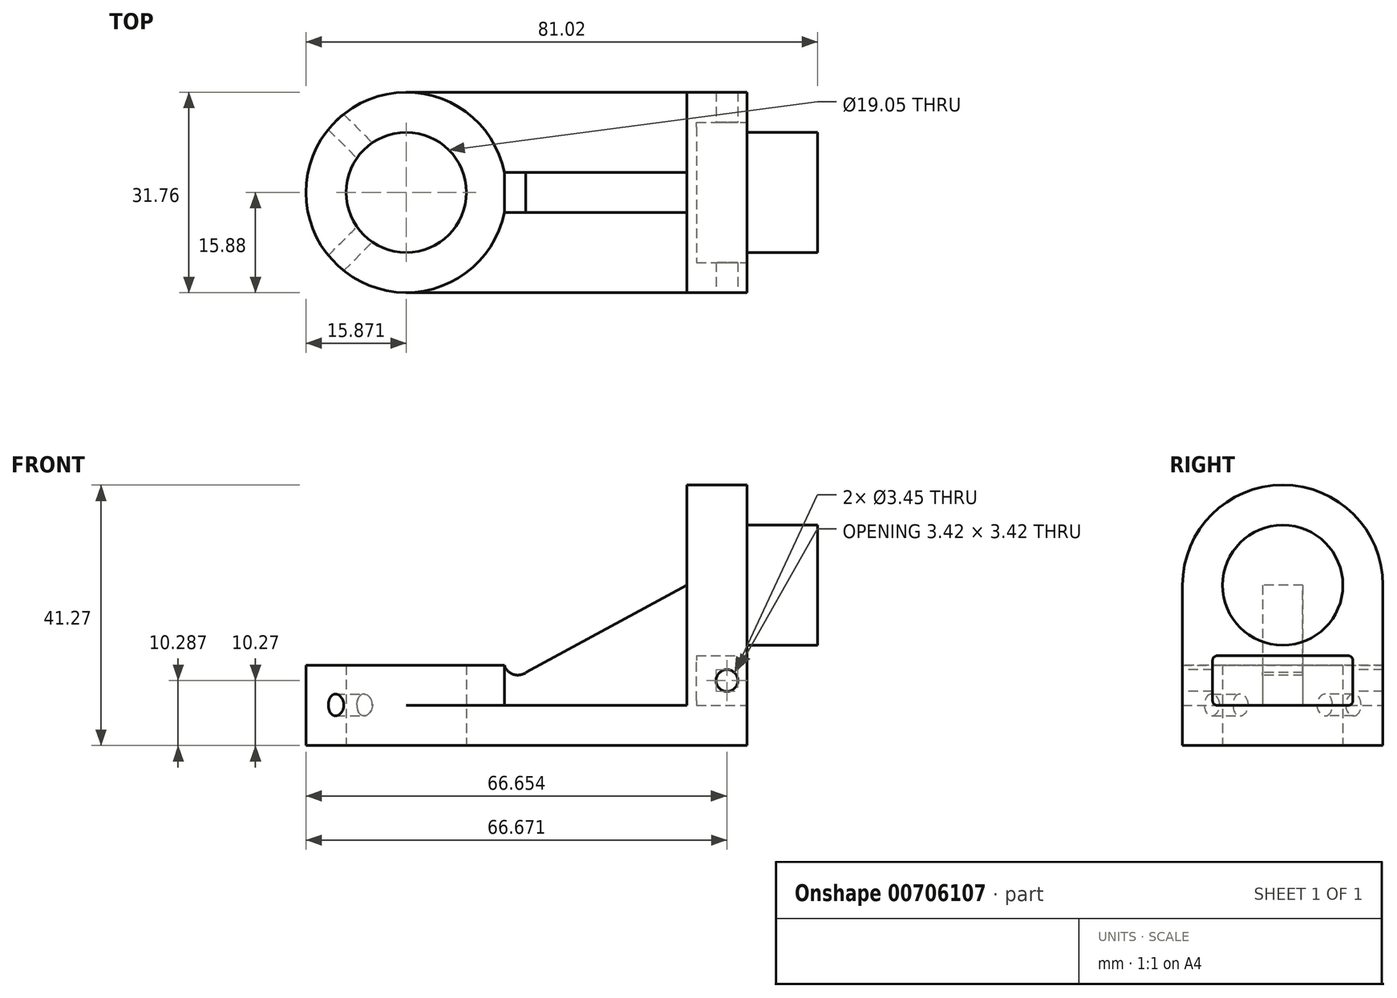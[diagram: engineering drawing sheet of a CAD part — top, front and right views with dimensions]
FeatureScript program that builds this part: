
annotation { "Feature Type Name" : "Feature", "Feature Type Description" : "" }
export const myFeature = defineFeature(function(context is Context, id is Id, definition is map)
    precondition{}
    {
        {
            var Q0;
            Q0=qCreatedBy(makeId("Top.planeOp"),FACE);
            var sketch = newSketch(context, id + "F0", { "sketchPlane" : qUnion([Q0])});
            skLineSegment(sketch, "E0.bottom", {"start": v(-25.39, -15.88) * mm, "end": v(28.59, -15.88) * mm});
            skLineSegment(sketch, "E0.top", {"start": v(-25.39, 15.87) * mm, "end": v(28.59, 15.87) * mm});
            skLineSegment(sketch, "E0.right", {"start": v(28.59, -15.88) * mm, "end": v(28.59, 15.87) * mm});
            skPoint(sketch, "E0.middle", {"position": v(1.6, 0) * mm});
            skArc(sketch, "E1", {"start": v(-25.39, 15.88) * mm, "mid": v(-41.26, 0) * mm, "end": v(-25.39, -15.88) * mm});
            skCircle(sketch, "E2", {"center": v(-25.39, 0) * mm, "radius": 9.53 * mm});
            skCircle(sketch, "E3", {"center": v(-25.39, 0) * mm, "radius": 15.88 * mm});
            skSolve(sketch);
        }
        {
            var Q0;
            Q0 = qSketchRegion(id + "F0", true);
            extrude(context, id + "F1", {"entities" : qUnion([Q0]), "depth" : 6.35 * mm, "offsetDistance" : 25.4 * mm});
        }
        {
            var Q0;
            Q0=makeQuery(id+"F1.opExtrude","CAP_FACE",FACE,{"disambiguationData":[OSD([sQuery(id+"F0.wireOp",EDGE,"E0.bottom"),sQuery(id+"F0.wireOp",EDGE,"E0.top"),sQuery(id+"F0.wireOp",EDGE,"E0.right"),sQuery(id+"F0.wireOp",EDGE,"E2"),sQuery(id+"F0.wireOp",EDGE,"E3")])],"isStart":false});
            var sketch = newSketch(context, id + "F2", { "sketchPlane" : qUnion([Q0])});
            skCircle(sketch, "E4", {"center": v(-25.39, 0) * mm, "radius": 9.53 * mm});
            skCircle(sketch, "E5", {"center": v(-25.39, 0) * mm, "radius": 15.88 * mm});
            skSolve(sketch);
        }
        {
            var Q0;
            Q0=makeQuery(id+"F2.imprint","IMPRINT",FACE,{"disambiguationData":[TD([[makeQuery(id+"F2.imprint","IMPRINT",EDGE,{"derivedFrom":sQuery(id+"F2.wireOp",EDGE,"E4")}),-1.0]])]});
            extrude(context, id + "F3", {"entities" : qUnion([Q0]), "operationType" : NewBodyOperationType.ADD, "depth" : 6.35 * mm, "offsetDistance" : 25.4 * mm});
        }
        {
            var Q0;
            Q0=makeQuery(id+"F1.opExtrude","SWEPT_FACE",FACE,{"disambiguationData":[OSD([sQuery(id+"F0.wireOp",EDGE,"E0.right")])]});
            var sketch = newSketch(context, id + "F4", { "sketchPlane" : qUnion([Q0])});
            skLineSegment(sketch, "E6.bottom", {"start": v(-15.88, 0) * mm, "end": v(15.87, 0) * mm});
            skLineSegment(sketch, "E6.left", {"start": v(-15.88, 0) * mm, "end": v(-15.88, 25.4) * mm});
            skLineSegment(sketch, "E6.right", {"start": v(15.87, 0) * mm, "end": v(15.87, 25.4) * mm});
            skArc(sketch, "E7", {"start": v(15.87, 25.4) * mm, "mid": v(0, 41.27) * mm, "end": v(-15.88, 25.4) * mm});
            skSolve(sketch);
        }
        {
            var Q0;
            Q0 = qSketchRegion(id + "F4", true);
            extrude(context, id + "F5", {"entities" : qUnion([Q0]), "operationType" : NewBodyOperationType.ADD, "oppositeDirection" : true, "depth" : 9.52 * mm, "offsetDistance" : 25.4 * mm});
        }
        {
            var Q0;
            Q0=makeQuery(id+"F5.boolean.opBoolean","MERGE",FACE,{"derivedFrom":[makeQuery(id+"F1.opExtrude","SWEPT_FACE",FACE,{"disambiguationData":[OSD([sQuery(id+"F0.wireOp",EDGE,"E0.right")])]}),makeQuery(id+"F5.opExtrude","CAP_FACE",FACE,{"disambiguationData":[OSD([sQuery(id+"F4.wireOp",EDGE,"E6.bottom"),sQuery(id+"F4.wireOp",EDGE,"E6.left"),sQuery(id+"F4.wireOp",EDGE,"E6.right"),sQuery(id+"F4.wireOp",EDGE,"E7")])],"isStart":true})]});
            var sketch = newSketch(context, id + "F6", { "sketchPlane" : qUnion([Q0])});
            skCircle(sketch, "E8", {"center": v(0, 25.4) * mm, "radius": 9.53 * mm});
            skSolve(sketch);
        }
        {
            var Q0;
            Q0 = qSketchRegion(id + "F6", true);
            extrude(context, id + "F7", {"entities" : qUnion([Q0]), "operationType" : NewBodyOperationType.ADD, "depth" : 11.18 * mm, "offsetDistance" : 25.4 * mm});
        }
        {
            var Q0;
            Q0=makeQuery(id+"F5.boolean.opBoolean","MERGE",FACE,{"derivedFrom":[makeQuery(id+"F1.opExtrude","SWEPT_FACE",FACE,{"disambiguationData":[OSD([sQuery(id+"F0.wireOp",EDGE,"E0.right")])]}),makeQuery(id+"F5.opExtrude","CAP_FACE",FACE,{"disambiguationData":[OSD([sQuery(id+"F4.wireOp",EDGE,"E6.bottom"),sQuery(id+"F4.wireOp",EDGE,"E6.left"),sQuery(id+"F4.wireOp",EDGE,"E6.right"),sQuery(id+"F4.wireOp",EDGE,"E7")])],"isStart":true})]});
            var sketch = newSketch(context, id + "F8", { "sketchPlane" : qUnion([Q0])});
            skLineSegment(sketch, "E9.bottom", {"start": v(10.35, 6.35) * mm, "end": v(-10.35, 6.35) * mm});
            skLineSegment(sketch, "E9.top", {"start": v(10.35, 14.22) * mm, "end": v(-10.35, 14.22) * mm});
            skLineSegment(sketch, "E9.left", {"start": v(11.11, 7.11) * mm, "end": v(11.11, 13.46) * mm});
            skLineSegment(sketch, "E9.right", {"start": v(-11.11, 7.11) * mm, "end": v(-11.11, 13.46) * mm});
            skPoint(sketch, "E9.middle", {"position": v(0, 10.29) * mm});
            skPoint(sketch, "E9.middle.positionSnap0", {"position": v(0, 0) * mm});
            skPoint(sketch, "E9.centerSnap0", {"position": v(0, 0) * mm});
            skPoint(sketch, "E10.visualSharp", {"position": v(-11.11, 6.35) * mm});
            skArc(sketch, "E10.filletArc", {"start": v(-11.11, 7.11) * mm, "mid": v(-10.89, 6.57) * mm, "end": v(-10.35, 6.35) * mm});
            skPoint(sketch, "E11.visualSharp", {"position": v(-11.11, 14.22) * mm});
            skArc(sketch, "E11.filletArc", {"start": v(-10.35, 14.22) * mm, "mid": v(-10.89, 14) * mm, "end": v(-11.11, 13.46) * mm});
            skPoint(sketch, "E12.visualSharp", {"position": v(11.11, 14.22) * mm});
            skArc(sketch, "E12.filletArc", {"start": v(11.11, 13.46) * mm, "mid": v(10.89, 14) * mm, "end": v(10.35, 14.22) * mm});
            skPoint(sketch, "E13.visualSharp", {"position": v(11.11, 6.35) * mm});
            skArc(sketch, "E13.filletArc", {"start": v(10.35, 6.35) * mm, "mid": v(10.89, 6.57) * mm, "end": v(11.11, 7.11) * mm});
            skSolve(sketch);
        }
        {
            var Q0;
            Q0 = qSketchRegion(id + "F8", true);
            extrude(context, id + "F9", {"entities" : qUnion([Q0]), "operationType" : NewBodyOperationType.REMOVE, "oppositeDirection" : true, "depth" : 8 * mm, "offsetDistance" : 25.4 * mm});
        }
        {
            var Q0;
            Q0=makeQuery(id+"F5.boolean.opBoolean","MERGE",FACE,{"derivedFrom":[makeQuery(id+"F1.opExtrude","SWEPT_FACE",FACE,{"disambiguationData":[OSD([sQuery(id+"F0.wireOp",EDGE,"E0.bottom")])]}),makeQuery(id+"F5.opExtrude","SWEPT_FACE",FACE,{"disambiguationData":[OSD([sQuery(id+"F4.wireOp",EDGE,"E6.left")])]})]});
            var sketch = newSketch(context, id + "F10", { "sketchPlane" : qUnion([Q0])});
            skCircle(sketch, "E14", {"center": v(25.41, 10.29) * mm, "radius": 1.73 * mm});
            skSolve(sketch);
        }
        {
            var Q0;
            Q0 = qSketchRegion(id + "F10", true);
            extrude(context, id + "F11", {"entities" : qUnion([Q0]), "operationType" : NewBodyOperationType.REMOVE, "oppositeDirection" : true, "depth" : 31.75 * mm, "offsetDistance" : 25.4 * mm});
        }
        {
            var Q0;
            Q0=qCreatedBy(makeId("Front.planeOp"),FACE);
            var sketch = newSketch(context, id + "F12", { "sketchPlane" : qUnion([Q0])});
            skLineSegment(sketch, "E15", {"start": v(19.06, 25.4) * mm, "end": v(-5.57, 8.75) * mm});
            skArc(sketch, "E16", {"start": v(-9.52, 10.76) * mm, "mid": v(-8.14, 8.6) * mm, "end": v(-5.57, 8.75) * mm});
            skLineSegment(sketch, "E17", {"start": v(-9.52, 10.76) * mm, "end": v(-9.52, 6.27) * mm});
            skLineSegment(sketch, "E18", {"start": v(-9.52, 6.27) * mm, "end": v(18.94, 6.27) * mm});
            skLineSegment(sketch, "E19", {"start": v(18.94, 6.27) * mm, "end": v(19.06, 25.4) * mm});
            skSolve(sketch);
        }
        {
            var Q0;
            Q0 = qSketchRegion(id + "F12", true);
            extrude(context, id + "F13", {"entities" : qUnion([Q0]), "endBound" : BoundingType.SYMMETRIC, "depth" : 6.35 * mm, "offsetDistance" : 25.4 * mm});
        }
        {
            var Q0;
            Q0 = qSketchRegion(id + "F12", true);
            extrude(context, id + "F14", {"entities" : qUnion([Q0]), "endBound" : BoundingType.SYMMETRIC, "depth" : 6.35 * mm, "offsetDistance" : 25.4 * mm});
        }
        {
            var Q0;
            Q0=qCreatedBy(makeId("Top.planeOp"),FACE);
            cPlane(context, id + "F15", {"entities" : qUnion([Q0]), "cplaneType" : CPlaneType.OFFSET, "offset" : 6.35 * mm, "width" : 152.4 * mm, "height" : 152.4 * mm});
        }
        {
            var Q0;
            Q0=makeQuery(id+"F5.opExtrude","CAP_FACE",FACE,{"disambiguationData":[OSD([sQuery(id+"F4.wireOp",EDGE,"E6.bottom"),sQuery(id+"F4.wireOp",EDGE,"E6.left"),sQuery(id+"F4.wireOp",EDGE,"E6.right"),sQuery(id+"F4.wireOp",EDGE,"E7")])],"isStart":false});
            cPlane(context, id + "F16", {"entities" : qUnion([Q0]), "cplaneType" : CPlaneType.OFFSET, "offset" : 55.88 * mm, "width" : 152.4 * mm, "height" : 152.4 * mm});
        }
        {
            var Q0;
            Q0=qCreatedBy(id+"F16.planeOp",FACE);
            var Q1;
            Q1=makeQuery(id+"F3.opExtrude","CAP_EDGE",EDGE,{"disambiguationData":[OSD([sQuery(id+"F2.wireOp",EDGE,"E5")])],"isStart":false});
            cPlane(context, id + "F17", {"entities" : qUnion([Q0, Q1]), "cplaneType" : CPlaneType.LINE_ANGLE, "offset" : 25.4 * mm, "angle" : 45 * degree, "width" : 152.4 * mm, "height" : 152.4 * mm});
        }
        {
            var Q0;
            Q0=qCreatedBy(id+"F16.planeOp",FACE);
            var Q1;
            Q1=makeQuery(id+"F3.opExtrude","CAP_EDGE",EDGE,{"disambiguationData":[OSD([sQuery(id+"F2.wireOp",EDGE,"E5")])],"isStart":false});
            cPlane(context, id + "F18", {"entities" : qUnion([Q0, Q1]), "cplaneType" : CPlaneType.LINE_ANGLE, "offset" : 25.4 * mm, "angle" : 45 * degree, "oppositeDirection" : true, "width" : 152.4 * mm, "height" : 152.4 * mm});
        }
        {
            var Q0;
            Q0=qCreatedBy(id+"F18.planeOp",FACE);
            var sketch = newSketch(context, id + "F19", { "sketchPlane" : qUnion([Q0])});
            skCircle(sketch, "E20", {"center": v(-17.92, 6.42) * mm, "radius": 1.73 * mm});
            skSolve(sketch);
        }
        {
            var Q0;
            Q0 = qSketchRegion(id + "F19", true);
            extrude(context, id + "F20", {"entities" : qUnion([Q0]), "operationType" : NewBodyOperationType.REMOVE, "oppositeDirection" : true, "depth" : 25.4 * mm, "offsetDistance" : 25.4 * mm});
        }
        {
            var Q0;
            Q0=qCreatedBy(id+"F17.planeOp",FACE);
            var sketch = newSketch(context, id + "F21", { "sketchPlane" : qUnion([Q0])});
            skCircle(sketch, "E21", {"center": v(17.9, 6.42) * mm, "radius": 1.73 * mm});
            skSolve(sketch);
        }
        {
            var Q0;
            Q0 = qSketchRegion(id + "F21", true);
            extrude(context, id + "F22", {"entities" : qUnion([Q0]), "operationType" : NewBodyOperationType.REMOVE, "oppositeDirection" : true, "depth" : 25.4 * mm, "offsetDistance" : 25.4 * mm});
        }
        {
            var Q0;
            Q0=makeQuery(id+"F13.opExtrude","SWEPT_BODY",BODY,{"disambiguationData":[OSD([sQuery(id+"F12.wireOp",EDGE,"E15"),sQuery(id+"F12.wireOp",EDGE,"E16"),sQuery(id+"F12.wireOp",EDGE,"E17"),sQuery(id+"F12.wireOp",EDGE,"E18"),sQuery(id+"F12.wireOp",EDGE,"E19")])]});
            deleteBodies(context, id + "F23", {"entities" : qUnion([Q0])});
        }
        {
            var Q0;
            Q0=makeQuery(id+"F14.opExtrude","SWEPT_BODY",BODY,{"disambiguationData":[OSD([sQuery(id+"F12.wireOp",EDGE,"E15"),sQuery(id+"F12.wireOp",EDGE,"E16"),sQuery(id+"F12.wireOp",EDGE,"E17"),sQuery(id+"F12.wireOp",EDGE,"E18"),sQuery(id+"F12.wireOp",EDGE,"E19")])]});
            deleteBodies(context, id + "F24", {"entities" : qUnion([Q0])});
        }
        {
            var Q0;
            Q0=makeQuery(id+"F1.opExtrude","CAP_FACE",FACE,{"disambiguationData":[OSD([sQuery(id+"F0.wireOp",EDGE,"E0.bottom"),sQuery(id+"F0.wireOp",EDGE,"E0.top"),sQuery(id+"F0.wireOp",EDGE,"E0.right"),sQuery(id+"F0.wireOp",EDGE,"E2"),sQuery(id+"F0.wireOp",EDGE,"E3")])],"isStart":false});
            var sketch = newSketch(context, id + "F25", { "sketchPlane" : qUnion([Q0])});
            skLineSegment(sketch, "E22", {"start": v(-9.51, 0) * mm, "end": v(19.06, 0) * mm, "construction": true});
            skLineSegment(sketch, "E23", {"start": v(-9.84, -3.18) * mm, "end": v(19.06, -3.18) * mm});
            skLineSegment(sketch, "E24.MirrorCS", {"start": v(-9.84, 3.18) * mm, "end": v(19.06, 3.18) * mm});
            skSolve(sketch);
        }
        {
            var Q0;
            Q0 = qSketchRegion(id + "F25", true);
            var Q1;
            {var subQ0=sQuery(id+"F25.wireOp",EDGE,"E23");Q1=makeQuery(id+"F25.imprint","IMPRINT",FACE,{"disambiguationData":[TD([[makeQuery(id+"F25.imprint","IMPRINT",EDGE,{"derivedFrom":subQ0}),1.0]])]});}
            extrude(context, id + "F26", {"entities" : qUnion([Q0, Q1]), "operationType" : NewBodyOperationType.ADD, "depth" : 25.4 * mm, "offsetDistance" : 25.4 * mm});
        }
        {
            var Q0;
            Q0=makeQuery(id+"F26.opExtrude","SWEPT_FACE",FACE,{"disambiguationData":[OSD([sQuery(id+"F25.wireOp",EDGE,"E23")])]});
            var sketch = newSketch(context, id + "F27", { "sketchPlane" : qUnion([Q0])});
            skLineSegment(sketch, "E25", {"start": v(19.06, 25.4) * mm, "end": v(-6.43, 11.54) * mm});
            skArc(sketch, "E26", {"start": v(-9.84, 12.7) * mm, "mid": v(-8.42, 11.27) * mm, "end": v(-6.43, 11.54) * mm});
            skPoint(sketch, "E26.first.point", {"position": v(-9.84, 12.7) * mm});
            skPoint(sketch, "E26.second.point", {"position": v(-6.43, 11.54) * mm});
            skPoint(sketch, "E26.third.point", {"position": v(-8.96, 11.54) * mm});
            skSolve(sketch);
        }
        {
            var Q0;
            Q0 = qSketchRegion(id + "F27", true);
            var Q1;
            {var subQ3=sQuery(id+"F27.wireOp",EDGE,"E25");Q1=makeQuery(id+"F27.imprint","IMPRINT",FACE,{"disambiguationData":[TD([[makeQuery(id+"F27.imprint","IMPRINT",EDGE,{"derivedFrom":subQ3}),-1.0]])]});}
            extrude(context, id + "F28", {"entities" : qUnion([Q0, Q1]), "operationType" : NewBodyOperationType.REMOVE, "oppositeDirection" : true, "depth" : 25.4 * mm, "offsetDistance" : 25.4 * mm});
        }
    });
